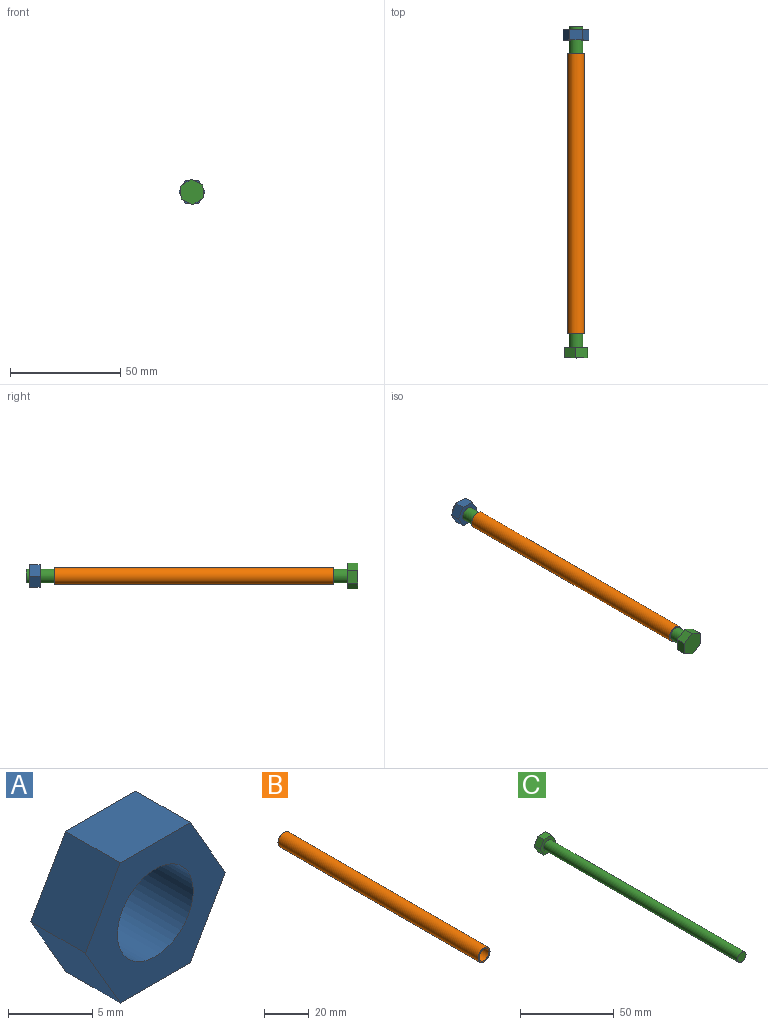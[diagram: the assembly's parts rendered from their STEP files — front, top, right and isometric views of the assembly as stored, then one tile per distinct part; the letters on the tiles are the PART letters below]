
ASSEMBLY  parts=3 mates=2
PART A: 9 faces, bbox 11.7x4.6x10.2 mm
  f0: plane 5.08x4.57mm, normal (0.87,0,0.5), area 26.8mm2, adj f1,f5,f6,f7
  f1: plane 5.87x4.57mm, normal (0,0,1), area 26.8mm2, adj f0,f2,f6,f7
  f2: plane 5.08x4.57mm, normal (-0.87,0,0.5), area 26.8mm2, adj f1,f3,f6,f7
  f3: plane 5.08x4.57mm, normal (-0.87,0,-0.5), area 26.8mm2, adj f2,f4,f6,f7
  f4: plane 5.87x4.57mm, normal (0,0,-1), area 26.8mm2, adj f3,f5,f6,f7
  f5: plane 5.08x4.57mm, normal (0.87,0,-0.5), area 26.8mm2, adj f0,f4,f6,f7
  f6: plane 11.73x10.16mm, normal (0,-1,0), area 57.7mm2, adj f0,f1,f2,f3,f4,f5,f8
  f7: plane 11.73x10.16mm, normal (0,1,0), area 57.7mm2, adj f0,f1,f2,f3,f4,f5,f8
  f8: cylinder r=3.17mm len=6.35mm, axis (0,1,0), area 91.2mm2, adj f6,f7
PART B: 4 faces, bbox 7.6x127x7.6 mm
  f0: cylinder r=3.81mm len=127mm, axis (0,1,0), area 3040.2mm2, adj f1,f2
  f1: plane 7.62x7.62mm, normal (0,-1,0), area 13.9mm2, adj f0,f3
  f2: plane 7.62x7.62mm, normal (0,1,0), area 13.9mm2, adj f0,f3
  f3: cylinder r=3.17mm len=127mm, axis (0,1,0), area 2533.5mm2, adj f1,f2
PART C: 10 faces, bbox 11.7x150.6x10.2 mm
  f0: cylinder r=3.17mm len=146.05mm, axis (0,-1,0), area 2913.6mm2, adj f1,f9
  f1: plane 6.35x6.35mm, normal (0,-1,0), area 31.7mm2, adj f0
  f2: plane 5.08x4.57mm, normal (-0.87,0,0.5), area 26.8mm2, adj f3,f7,f8,f9
  f3: plane 5.87x4.57mm, normal (0,0,1), area 26.8mm2, adj f2,f4,f8,f9
  f4: plane 5.08x4.57mm, normal (0.87,0,0.5), area 26.8mm2, adj f3,f5,f8,f9
  f5: plane 5.08x4.57mm, normal (0.87,0,-0.5), area 26.8mm2, adj f4,f6,f8,f9
  f6: plane 5.87x4.57mm, normal (0,0,-1), area 26.8mm2, adj f5,f7,f8,f9
  f7: plane 5.08x4.57mm, normal (-0.87,0,-0.5), area 26.8mm2, adj f2,f6,f8,f9
  f8: plane 11.73x10.16mm, normal (0,1,0), area 89.4mm2, adj f2,f3,f4,f5,f6,f7
  f9: plane 11.73x10.16mm, normal (0,-1,0), area 57.7mm2, adj f0,f2,f3,f4,f5,f6,f7
PLACE A t=(-13.79,33.6,-3.6)mm
PLACE B t=(-13.79,-40.82,-3.6)mm
PLACE C rot(axis=(0.29,0,-0.96),180deg) t=(-13.79,-37.64,-3.6)mm
MATE revolute B.f0 <-> C.f0  axis (0,1,0) through (-13.79,-104.32,-3.6)mm
MATE revolute A.f8 <-> B.f0  axis (0,-1,0) through (-13.79,29.03,-3.6)mm
